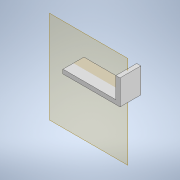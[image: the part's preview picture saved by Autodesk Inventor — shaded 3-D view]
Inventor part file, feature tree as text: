
AUTODESK INVENTOR PART (.ipt)
format: ipt  version: 2020 (Build 240168000, 168)  size: 113,664 bytes
history: native  units: mm
features: hole x2, sketch x2, plane x1, extrude x1
ambient origin geometry x8: Origin, YZ Plane, XZ Plane, XY Plane, X Axis, Y Axis, Z Axis, Center Point
bodies: Solid1 (feature_tree)
feature tree (6):
  plane  "Work Plane1"
  extrude  "Extrusion1"  Depth=10.0mm
  hole  "Hole2"  [1 undecoded]
  sketch  "Sketch1"  dims[d2=50.0mm d3=0.0mm]
  sketch  "Sketch2"  dims[d4=6.6mm d5=6.0mm d6=16.0mm d7=8.0mm d8=90.0deg d9=8.0mm d10=0.0mm d11=10.0mm d12=10.0mm d13=60.0mm d15=10.0mm]
  hole  "Hole1"  [1 undecoded]
note: 2 required parameter values undecoded (feature->parameter linkage not recoverable at this tier; creation-order binding heuristic only, values carry confidence <= 0.55)
